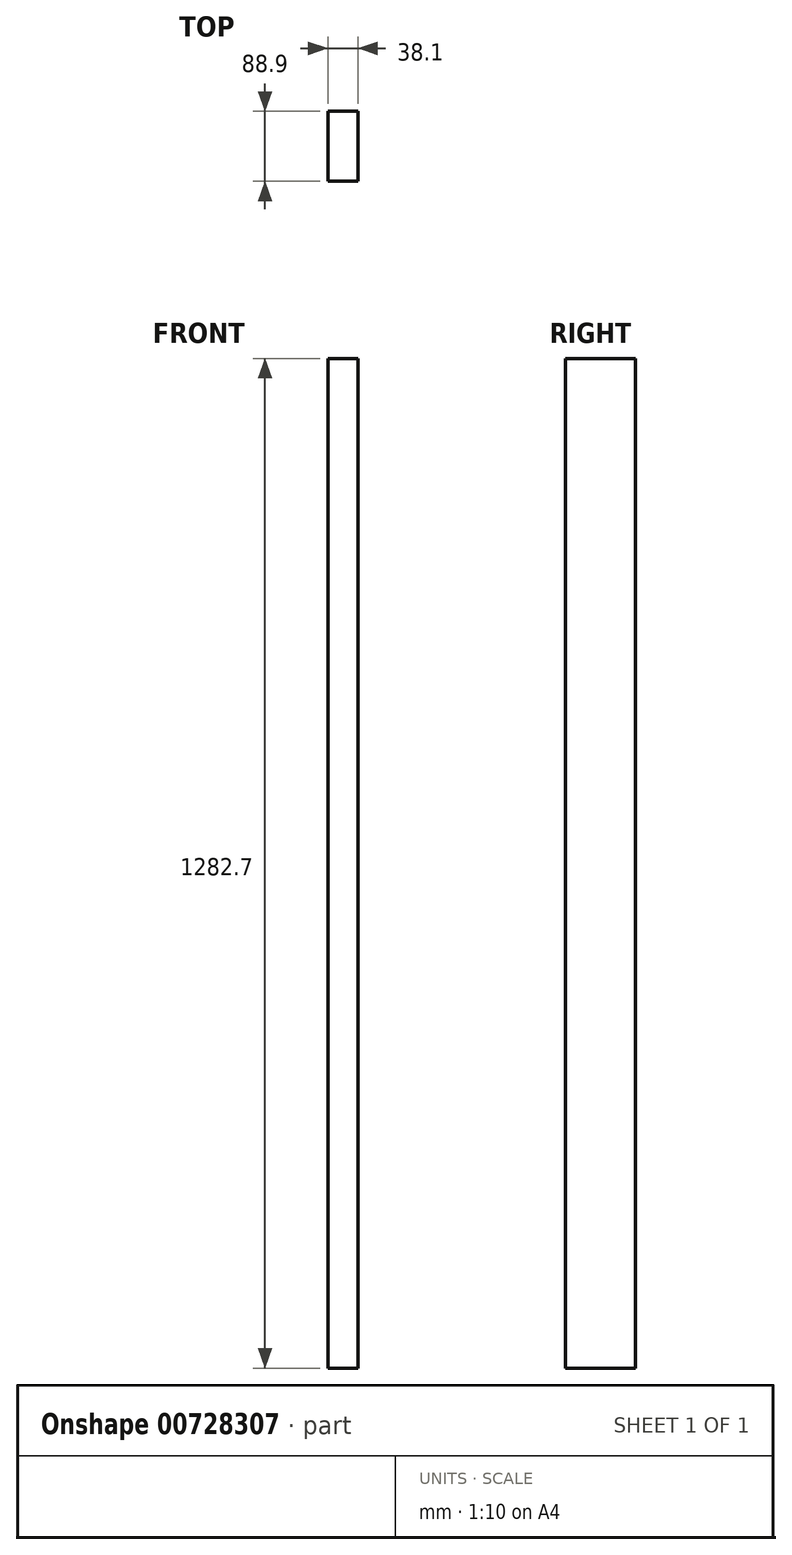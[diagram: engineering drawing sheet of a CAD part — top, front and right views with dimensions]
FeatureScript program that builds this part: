
annotation { "Feature Type Name" : "Feature", "Feature Type Description" : "" }
export const myFeature = defineFeature(function(context is Context, id is Id, definition is map)
    precondition{}
    {
        {
            var Q0;
            Q0=qCreatedBy(makeId("Front.planeOp"),FACE);
            var sketch = newSketch(context, id + "F0", { "sketchPlane" : qUnion([Q0])});
            skLineSegment(sketch, "E0.bottom", {"start": v(-19.05, -641.35) * mm, "end": v(19.05, -641.35) * mm});
            skLineSegment(sketch, "E0.top", {"start": v(-19.05, 641.35) * mm, "end": v(19.05, 641.35) * mm});
            skLineSegment(sketch, "E0.left", {"start": v(-19.05, -641.35) * mm, "end": v(-19.05, 641.35) * mm});
            skLineSegment(sketch, "E0.right", {"start": v(19.05, -641.35) * mm, "end": v(19.05, 641.35) * mm});
            skPoint(sketch, "E0.middle", {"position": v(0, 0) * mm});
            skSolve(sketch);
        }
        {
            var Q0;
            Q0=qSketchRegion(id+"F0",true);
            extrude(context, id + "F1", {"entities" : qUnion([Q0]), "depth" : 88.9 * mm, "offsetDistance" : 25.4 * mm});
        }
    });
